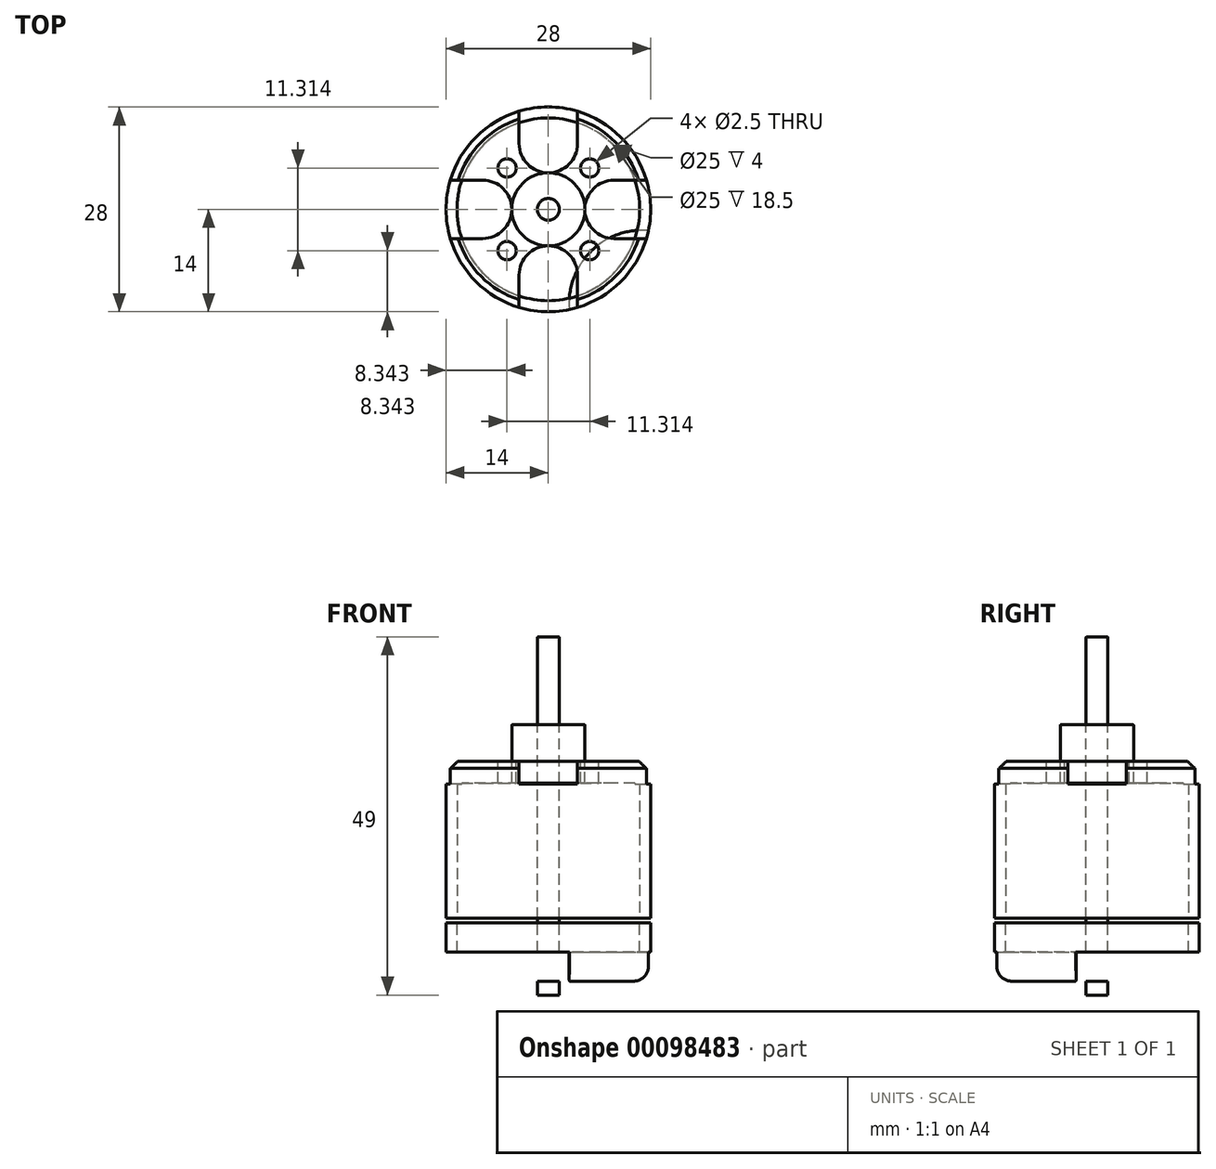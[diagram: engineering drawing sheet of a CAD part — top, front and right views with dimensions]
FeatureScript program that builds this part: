
annotation { "Feature Type Name" : "Feature", "Feature Type Description" : "" }
export const myFeature = defineFeature(function(context is Context, id is Id, definition is map)
    precondition{}
    {
        {
            var Q0;
            Q0=qCreatedBy(makeId("Top.planeOp"),FACE);
            var sketch = newSketch(context, id + "F0", { "sketchPlane" : qUnion([Q0])});
            skCircle(sketch, "E0", {"center": v(0, 0) * mm, "radius": 14 * mm});
            skSolve(sketch);
        }
        {
            var Q0;
            Q0=qSketchRegion(id+"F0",true);
            extrude(context, id + "F1", {"entities" : qUnion([Q0]), "depth" : 21.5 * mm});
        }
        {
            var Q0;
            Q0=makeQuery(id+"F1.opExtrude","CAP_FACE",FACE,{"disambiguationData":[OSD([sQuery(id+"F0.wireOp",EDGE,"E0")])],"isStart":false});
            var sketch = newSketch(context, id + "F2", { "sketchPlane" : qUnion([Q0])});
            skCircle(sketch, "E1", {"center": v(0, 0) * mm, "radius": 5 * mm});
            skSolve(sketch);
        }
        {
            var Q0;
            Q0=qSketchRegion(id+"F2",true);
            extrude(context, id + "F3", {"entities" : qUnion([Q0]), "depth" : 5 * mm});
        }
        {
            var Q0;
            Q0=makeQuery(id+"F1.opExtrude","CAP_FACE",FACE,{"disambiguationData":[OSD([sQuery(id+"F0.wireOp",EDGE,"E0")])],"isStart":true});
            var sketch = newSketch(context, id + "F4", { "sketchPlane" : qUnion([Q0])});
            skCircle(sketch, "E2", {"center": v(0, 0) * mm, "radius": 12.5 * mm});
            skSolve(sketch);
        }
        {
            var Q0;
            Q0=qSketchRegion(id+"F4",true);
            extrude(context, id + "F5", {"entities" : qUnion([Q0]), "operationType" : NewBodyOperationType.REMOVE, "oppositeDirection" : true, "depth" : 18.5 * mm});
        }
        {
            var Q0;
            Q0=makeQuery(id+"F3.opExtrude","CAP_FACE",FACE,{"disambiguationData":[OSD([sQuery(id+"F2.wireOp",EDGE,"E1")])],"isStart":false});
            cPlane(context, id + "F6", {"entities" : qUnion([Q0]), "cplaneType" : CPlaneType.OFFSET, "offset" : 12 * mm, "width" : 150 * mm, "height" : 150 * mm});
        }
        {
            var Q0;
            Q0=qCreatedBy(id+"F6.planeOp",FACE);
            var sketch = newSketch(context, id + "F7", { "sketchPlane" : qUnion([Q0])});
            skCircle(sketch, "E3", {"center": v(0, 0) * mm, "radius": 1.5 * mm});
            skSolve(sketch);
        }
        {
            var Q0;
            Q0=qSketchRegion(id+"F7",true);
            extrude(context, id + "F8", {"entities" : qUnion([Q0]), "oppositeDirection" : true, "depth" : 49 * mm});
        }
        {
            var Q0;
            Q0=makeQuery(id+"F1.opExtrude","CAP_FACE",FACE,{"disambiguationData":[OSD([sQuery(id+"F0.wireOp",EDGE,"E0")])],"isStart":false});
            var sketch = newSketch(context, id + "F9", { "sketchPlane" : qUnion([Q0])});
            skArc(sketch, "E4", {"start": v(-4, 9) * mm, "mid": v(0, 5) * mm, "end": v(4, 9) * mm});
            skLineSegment(sketch, "E5", {"start": v(4, 9) * mm, "end": v(4, 13.42) * mm});
            skLineSegment(sketch, "E6.MirrorCS", {"start": v(-4, 9) * mm, "end": v(-4, 13.42) * mm});
            skArc(sketch, "E7", {"start": v(-4, 13.42) * mm, "mid": v(0, 14) * mm, "end": v(4, 13.42) * mm});
            skArc(sketch, "E8.1.0", {"start": v(-9, -4) * mm, "mid": v(-5, 0) * mm, "end": v(-9, 4) * mm});
            skLineSegment(sketch, "E8.1.1", {"start": v(-9, 4) * mm, "end": v(-13.42, 4) * mm});
            skArc(sketch, "E8.1.2", {"start": v(-13.42, -4) * mm, "mid": v(-14, 0) * mm, "end": v(-13.42, 4) * mm});
            skLineSegment(sketch, "E8.1.3", {"start": v(-9, -4) * mm, "end": v(-13.42, -4) * mm});
            skArc(sketch, "E8.2.0", {"start": v(4, -9) * mm, "mid": v(0, -5) * mm, "end": v(-4, -9) * mm});
            skLineSegment(sketch, "E8.2.1", {"start": v(-4, -9) * mm, "end": v(-4, -13.42) * mm});
            skArc(sketch, "E8.2.2", {"start": v(4, -13.42) * mm, "mid": v(0, -14) * mm, "end": v(-4, -13.42) * mm});
            skLineSegment(sketch, "E8.2.3", {"start": v(4, -9) * mm, "end": v(4, -13.42) * mm});
            skArc(sketch, "E8.3.0", {"start": v(9, 4) * mm, "mid": v(5, 0) * mm, "end": v(9, -4) * mm});
            skLineSegment(sketch, "E8.3.1", {"start": v(9, -4) * mm, "end": v(13.42, -4) * mm});
            skArc(sketch, "E8.3.2", {"start": v(13.42, 4) * mm, "mid": v(14, 0) * mm, "end": v(13.42, -4) * mm});
            skLineSegment(sketch, "E8.3.3", {"start": v(9, 4) * mm, "end": v(13.42, 4) * mm});
            skSolve(sketch);
        }
        {
            var Q0;
            Q0=qSketchRegion(id+"F9",true);
            extrude(context, id + "F10", {"entities" : qUnion([Q0]), "operationType" : NewBodyOperationType.REMOVE, "oppositeDirection" : true, "depth" : 3.12 * mm});
        }
        {
            var Q0;
            {var subQ0=sQuery(id+"F0.wireOp",EDGE,"E0");Q0=makeQuery(id+"F10.boolean.opBoolean","SPLIT",EDGE,{"disambiguationData":[TD([makeQuery(id+"F10.opExtrude","SWEPT_FACE",FACE,{"disambiguationData":[OSD([sQuery(id+"F9.wireOp",EDGE,"E6.MirrorCS")])]})])],"derivedFrom":makeQuery(id+"F1.opExtrude","CAP_EDGE",EDGE,{"disambiguationData":[OSD([subQ0])],"isStart":false})});}
            var Q1;
            {var subQ0=sQuery(id+"F0.wireOp",EDGE,"E0");Q1=makeQuery(id+"F10.boolean.opBoolean","SPLIT",EDGE,{"disambiguationData":[TD([makeQuery(id+"F10.opExtrude","SWEPT_FACE",FACE,{"disambiguationData":[OSD([sQuery(id+"F9.wireOp",EDGE,"E5")])]})])],"derivedFrom":makeQuery(id+"F1.opExtrude","CAP_EDGE",EDGE,{"disambiguationData":[OSD([subQ0])],"isStart":false})});}
            var Q2;
            {var subQ0=sQuery(id+"F0.wireOp",EDGE,"E0");Q2=makeQuery(id+"F10.boolean.opBoolean","SPLIT",EDGE,{"disambiguationData":[TD([makeQuery(id+"F10.opExtrude","SWEPT_FACE",FACE,{"disambiguationData":[OSD([sQuery(id+"F9.wireOp",EDGE,"E8.2.3")])]})])],"derivedFrom":makeQuery(id+"F1.opExtrude","CAP_EDGE",EDGE,{"disambiguationData":[OSD([subQ0])],"isStart":false})});}
            var Q3;
            {var subQ0=sQuery(id+"F0.wireOp",EDGE,"E0");Q3=makeQuery(id+"F10.boolean.opBoolean","SPLIT",EDGE,{"disambiguationData":[TD([makeQuery(id+"F10.opExtrude","SWEPT_FACE",FACE,{"disambiguationData":[OSD([sQuery(id+"F9.wireOp",EDGE,"E8.1.3")])]})])],"derivedFrom":makeQuery(id+"F1.opExtrude","CAP_EDGE",EDGE,{"disambiguationData":[OSD([subQ0])],"isStart":false})});}
            chamfer(context, id + "F11", {"entities" : qUnion([Q0, Q1, Q2, Q3]), "width" : 1 * mm, "tangentPropagation" : true});
        }
        {
            var Q0;
            Q0=makeQuery(id+"F8.opExtrude","CAP_EDGE",EDGE,{"disambiguationData":[OSD([sQuery(id+"F7.wireOp",EDGE,"E3")])],"isStart":true});
            fillet(context, id + "F12", {"entities" : qUnion([Q0]), "radius" : .1 * mm, "tangentPropagation" : true, "allowEdgeOverflow" : false});
        }
        {
            var Q0;
            Q0=makeQuery(id+"F3.opExtrude","CAP_EDGE",EDGE,{"disambiguationData":[OSD([sQuery(id+"F2.wireOp",EDGE,"E1")])],"isStart":false});
            var Q1;
            Q1=makeQuery(id+"F3.opExtrude","CAP_EDGE",EDGE,{"disambiguationData":[OSD([sQuery(id+"F2.wireOp",EDGE,"E1")])],"isStart":true});
            fillet(context, id + "F13", {"entities" : qUnion([Q0, Q1]), "radius" : .1 * mm, "tangentPropagation" : true, "allowEdgeOverflow" : false});
        }
        {
            var Q0;
            Q0=makeQuery(id+"F1.opExtrude","CAP_FACE",FACE,{"disambiguationData":[OSD([sQuery(id+"F0.wireOp",EDGE,"E0")])],"isStart":true});
            var sketch = newSketch(context, id + "F14", { "sketchPlane" : qUnion([Q0])});
            skCircle(sketch, "E9.0", {"center": v(0, 0) * mm, "radius": 14 * mm});
            skCircle(sketch, "E9.1", {"center": v(0, 0) * mm, "radius": 12.5 * mm});
            skSolve(sketch);
        }
        {
            var Q0;
            Q0=qSketchRegion(id+"F14",true);
            extrude(context, id + "F15", {"entities" : qUnion([Q0]), "depth" : 8 * mm});
        }
        {
            var Q0;
            Q0=makeQuery(id+"F15.opExtrude","SWEPT_BODY",BODY,{"disambiguationData":[OSD([sQuery(id+"F14.wireOp",EDGE,"E9.0"),sQuery(id+"F14.wireOp",EDGE,"E9.1")])]});
            transform(context, id + "F16", {"entities" : qUnion([Q0]), "transformType" : TransformType.TRANSLATION_3D, "dx" : 0 * mm, "dy" : 0 * mm, "dz" : -.6 * mm, "makeCopy" : false});
        }
        {
            var Q0;
            Q0=makeQuery(id+"F15.opExtrude","CAP_FACE",FACE,{"disambiguationData":[OSD([sQuery(id+"F14.wireOp",EDGE,"E9.0"),sQuery(id+"F14.wireOp",EDGE,"E9.1")])],"isStart":false});
            var sketch = newSketch(context, id + "F17", { "sketchPlane" : qUnion([Q0])});
            skCircle(sketch, "E10.0", {"center": v(0, 0) * mm, "radius": 12.5 * mm});
            skCircle(sketch, "E11", {"center": v(0, 0) * mm, "radius": 8 * mm, "construction": true});
            skCircle(sketch, "E12", {"center": v(-8, 0) * mm, "radius": 1.25 * mm});
            skCircle(sketch, "E13.1.0", {"center": v(0, -8) * mm, "radius": 1.25 * mm});
            skCircle(sketch, "E13.2.0", {"center": v(8, 0) * mm, "radius": 1.25 * mm});
            skCircle(sketch, "E13.3.0", {"center": v(0, 8) * mm, "radius": 1.25 * mm});
            skSolve(sketch);
        }
        {
            var Q0;
            Q0=qSketchRegion(id+"F17",true);
            extrude(context, id + "F18", {"entities" : qUnion([Q0]), "oppositeDirection" : true, "depth" : 4 * mm});
        }
        {
            var Q0;
            Q0=makeQuery(id+"F18.opExtrude","SWEPT_BODY",BODY,{"disambiguationData":[OSD([sQuery(id+"F17.wireOp",EDGE,"E10.0")])]});
            var Q1;
            Q1=makeQuery(id+"F15.opExtrude","SWEPT_BODY",BODY,{"disambiguationData":[OSD([sQuery(id+"F14.wireOp",EDGE,"E9.0"),sQuery(id+"F14.wireOp",EDGE,"E9.1")])]});
            booleanBodies(context, id + "F19", {"operationType" : BooleanOperationType.UNION, "tools" : qUnion([Q0, Q1])});
        }
        {
            var Q0;
            Q0=makeQuery(id+"F19.opBoolean","MERGE",FACE,{"derivedFrom":[makeQuery(id+"F15.opExtrude","CAP_FACE",FACE,{"disambiguationData":[OSD([sQuery(id+"F14.wireOp",EDGE,"E9.0"),sQuery(id+"F14.wireOp",EDGE,"E9.1")])],"isStart":false}),makeQuery(id+"F18.opExtrude","CAP_FACE",FACE,{"disambiguationData":[OSD([sQuery(id+"F17.wireOp",EDGE,"E10.0"),sQuery(id+"F17.wireOp",EDGE,"E12"),sQuery(id+"F17.wireOp",EDGE,"E13.1.0"),sQuery(id+"F17.wireOp",EDGE,"E13.2.0"),sQuery(id+"F17.wireOp",EDGE,"E13.3.0")])],"isStart":true})]});
            var sketch = newSketch(context, id + "F20", { "sketchPlane" : qUnion([Q0])});
            skLineSegment(sketch, "E14", {"start": v(0, 0) * mm, "end": v(-16.49, 16.49) * mm, "construction": true});
            skArc(sketch, "E15", {"start": v(-13.7, 2.88) * mm, "mid": v(-5.79, 5.79) * mm, "end": v(-2.88, 13.7) * mm});
            skLineSegment(sketch, "E16", {"start": v(-2.85, 0) * mm, "end": v(-2.85, 15.2) * mm, "construction": true});
            skArc(sketch, "E17", {"start": v(-13.7, 2.88) * mm, "mid": v(-9.9, 9.9) * mm, "end": v(-2.88, 13.7) * mm});
            skArc(sketch, "E18.MirrorCS", {"start": v(13.7, 2.88) * mm, "mid": v(5.79, 5.79) * mm, "end": v(2.88, 13.7) * mm});
            skArc(sketch, "E19.MirrorCS", {"start": v(13.7, 2.88) * mm, "mid": v(9.9, 9.9) * mm, "end": v(2.88, 13.7) * mm});
            skArc(sketch, "E20.MirrorCS", {"start": v(-13.7, -2.88) * mm, "mid": v(-9.9, -9.9) * mm, "end": v(-2.88, -13.7) * mm});
            skArc(sketch, "E21.MirrorCS", {"start": v(-13.7, -2.88) * mm, "mid": v(-5.79, -5.79) * mm, "end": v(-2.88, -13.7) * mm});
            skArc(sketch, "E22.MirrorCS", {"start": v(13.7, -2.88) * mm, "mid": v(5.79, -5.79) * mm, "end": v(2.88, -13.7) * mm});
            skArc(sketch, "E23.MirrorCS", {"start": v(13.7, -2.88) * mm, "mid": v(9.9, -9.9) * mm, "end": v(2.88, -13.7) * mm});
            skSolve(sketch);
        }
        {
            var Q0;
            Q0=makeQuery(id+"F20.imprint","IMPRINT",FACE,{"disambiguationData":[TD([[makeQuery(id+"F20.imprint","IMPRINT",EDGE,{"derivedFrom":sQuery(id+"F20.wireOp",EDGE,"E15")}),1.0]])]});
            var Q1;
            Q1=makeQuery(id+"F20.imprint","IMPRINT",FACE,{"disambiguationData":[TD([[makeQuery(id+"F20.imprint","IMPRINT",EDGE,{"derivedFrom":sQuery(id+"F20.wireOp",EDGE,"E18.MirrorCS")}),-1.0]])]});
            var Q2;
            Q2=makeQuery(id+"F20.imprint","IMPRINT",FACE,{"disambiguationData":[TD([[makeQuery(id+"F20.imprint","IMPRINT",EDGE,{"derivedFrom":sQuery(id+"F20.wireOp",EDGE,"E20.MirrorCS")}),-1.0]])]});
            var Q3;
            Q3=makeQuery(id+"F20.imprint","IMPRINT",FACE,{"disambiguationData":[TD([[makeQuery(id+"F20.imprint","IMPRINT",EDGE,{"derivedFrom":sQuery(id+"F20.wireOp",EDGE,"E22.MirrorCS")}),1.0]])]});
            extrude(context, id + "F21", {"entities" : qUnion([Q0, Q1, Q2, Q3]), "operationType" : NewBodyOperationType.REMOVE, "oppositeDirection" : true, "depth" : 4 * mm});
        }
        {
            var Q0;
            {var subQ0=sQuery(id+"F14.wireOp",EDGE,"E9.0");Q0=makeQuery(id+"F21.boolean.opBoolean","SPLIT",EDGE,{"disambiguationData":[TD([makeQuery(id+"F15.opExtrude","SWEPT_FACE",FACE,{"disambiguationData":[OSD([subQ0])]}),makeQuery(id+"F15.opExtrude","CAP_FACE",FACE,{"disambiguationData":[OSD([subQ0,sQuery(id+"F14.wireOp",EDGE,"E9.1")])],"isStart":false}),makeQuery(id+"F18.opExtrude","CAP_FACE",FACE,{"disambiguationData":[OSD([sQuery(id+"F17.wireOp",EDGE,"E10.0"),sQuery(id+"F17.wireOp",EDGE,"E12"),sQuery(id+"F17.wireOp",EDGE,"E13.1.0"),sQuery(id+"F17.wireOp",EDGE,"E13.2.0"),sQuery(id+"F17.wireOp",EDGE,"E13.3.0")])],"isStart":true}),makeQuery(id+"F21.opExtrude","SWEPT_FACE",FACE,{"disambiguationData":[OSD([sQuery(id+"F20.wireOp",EDGE,"E15")])]}),makeQuery(id+"F21.opExtrude","SWEPT_FACE",FACE,{"disambiguationData":[OSD([sQuery(id+"F20.wireOp",EDGE,"E21.MirrorCS")])]})])],"derivedFrom":makeQuery(id+"F15.opExtrude","CAP_EDGE",EDGE,{"disambiguationData":[OSD([subQ0])],"isStart":false})});}
            var Q1;
            {var subQ0=sQuery(id+"F14.wireOp",EDGE,"E9.0");Q1=makeQuery(id+"F21.boolean.opBoolean","SPLIT",EDGE,{"disambiguationData":[TD([makeQuery(id+"F15.opExtrude","SWEPT_FACE",FACE,{"disambiguationData":[OSD([subQ0])]}),makeQuery(id+"F15.opExtrude","CAP_FACE",FACE,{"disambiguationData":[OSD([subQ0,sQuery(id+"F14.wireOp",EDGE,"E9.1")])],"isStart":false}),makeQuery(id+"F18.opExtrude","CAP_FACE",FACE,{"disambiguationData":[OSD([sQuery(id+"F17.wireOp",EDGE,"E10.0"),sQuery(id+"F17.wireOp",EDGE,"E12"),sQuery(id+"F17.wireOp",EDGE,"E13.1.0"),sQuery(id+"F17.wireOp",EDGE,"E13.2.0"),sQuery(id+"F17.wireOp",EDGE,"E13.3.0")])],"isStart":true}),makeQuery(id+"F21.opExtrude","SWEPT_FACE",FACE,{"disambiguationData":[OSD([sQuery(id+"F20.wireOp",EDGE,"E15")])]}),makeQuery(id+"F21.opExtrude","SWEPT_FACE",FACE,{"disambiguationData":[OSD([sQuery(id+"F20.wireOp",EDGE,"E18.MirrorCS")])]})])],"derivedFrom":makeQuery(id+"F15.opExtrude","CAP_EDGE",EDGE,{"disambiguationData":[OSD([subQ0])],"isStart":false})});}
            var Q2;
            {var subQ0=sQuery(id+"F14.wireOp",EDGE,"E9.0");Q2=makeQuery(id+"F21.boolean.opBoolean","SPLIT",EDGE,{"disambiguationData":[TD([makeQuery(id+"F15.opExtrude","SWEPT_FACE",FACE,{"disambiguationData":[OSD([subQ0])]}),makeQuery(id+"F15.opExtrude","CAP_FACE",FACE,{"disambiguationData":[OSD([subQ0,sQuery(id+"F14.wireOp",EDGE,"E9.1")])],"isStart":false}),makeQuery(id+"F18.opExtrude","CAP_FACE",FACE,{"disambiguationData":[OSD([sQuery(id+"F17.wireOp",EDGE,"E10.0"),sQuery(id+"F17.wireOp",EDGE,"E12"),sQuery(id+"F17.wireOp",EDGE,"E13.1.0"),sQuery(id+"F17.wireOp",EDGE,"E13.2.0"),sQuery(id+"F17.wireOp",EDGE,"E13.3.0")])],"isStart":true}),makeQuery(id+"F21.opExtrude","SWEPT_FACE",FACE,{"disambiguationData":[OSD([sQuery(id+"F20.wireOp",EDGE,"E18.MirrorCS")])]}),makeQuery(id+"F21.opExtrude","SWEPT_FACE",FACE,{"disambiguationData":[OSD([sQuery(id+"F20.wireOp",EDGE,"E22.MirrorCS")])]})])],"derivedFrom":makeQuery(id+"F15.opExtrude","CAP_EDGE",EDGE,{"disambiguationData":[OSD([subQ0])],"isStart":false})});}
            var Q3;
            {var subQ0=sQuery(id+"F14.wireOp",EDGE,"E9.0");Q3=makeQuery(id+"F21.boolean.opBoolean","SPLIT",EDGE,{"disambiguationData":[TD([makeQuery(id+"F15.opExtrude","SWEPT_FACE",FACE,{"disambiguationData":[OSD([subQ0])]}),makeQuery(id+"F15.opExtrude","CAP_FACE",FACE,{"disambiguationData":[OSD([subQ0,sQuery(id+"F14.wireOp",EDGE,"E9.1")])],"isStart":false}),makeQuery(id+"F18.opExtrude","CAP_FACE",FACE,{"disambiguationData":[OSD([sQuery(id+"F17.wireOp",EDGE,"E10.0"),sQuery(id+"F17.wireOp",EDGE,"E12"),sQuery(id+"F17.wireOp",EDGE,"E13.1.0"),sQuery(id+"F17.wireOp",EDGE,"E13.2.0"),sQuery(id+"F17.wireOp",EDGE,"E13.3.0")])],"isStart":true}),makeQuery(id+"F21.opExtrude","SWEPT_FACE",FACE,{"disambiguationData":[OSD([sQuery(id+"F20.wireOp",EDGE,"E21.MirrorCS")])]}),makeQuery(id+"F21.opExtrude","SWEPT_FACE",FACE,{"disambiguationData":[OSD([sQuery(id+"F20.wireOp",EDGE,"E22.MirrorCS")])]})])],"derivedFrom":makeQuery(id+"F15.opExtrude","CAP_EDGE",EDGE,{"disambiguationData":[OSD([subQ0])],"isStart":false})});}
            fillet(context, id + "F22", {"entities" : qUnion([Q0, Q1, Q2, Q3]), "radius" : 2 * mm, "tangentPropagation" : true, "allowEdgeOverflow" : false});
        }
        {
            var Q0;
            Q0=makeQuery(id+"F19.opBoolean","MERGE",FACE,{"derivedFrom":[makeQuery(id+"F15.opExtrude","CAP_FACE",FACE,{"disambiguationData":[OSD([sQuery(id+"F14.wireOp",EDGE,"E9.0"),sQuery(id+"F14.wireOp",EDGE,"E9.1")])],"isStart":false}),makeQuery(id+"F18.opExtrude","CAP_FACE",FACE,{"disambiguationData":[OSD([sQuery(id+"F17.wireOp",EDGE,"E10.0"),sQuery(id+"F17.wireOp",EDGE,"E12"),sQuery(id+"F17.wireOp",EDGE,"E13.1.0"),sQuery(id+"F17.wireOp",EDGE,"E13.2.0"),sQuery(id+"F17.wireOp",EDGE,"E13.3.0")])],"isStart":true})]});
            var sketch = newSketch(context, id + "F23", { "sketchPlane" : qUnion([Q0])});
            skCircle(sketch, "E24", {"center": v(0, 0) * mm, "radius": 5 * mm});
            skCircle(sketch, "E25", {"center": v(0, 0) * mm, "radius": 1.5 * mm});
            skSolve(sketch);
        }
        {
            var Q0;
            Q0=qSketchRegion(id+"F23",true);
            extrude(context, id + "F24", {"entities" : qUnion([Q0]), "operationType" : NewBodyOperationType.REMOVE, "oppositeDirection" : true, "depth" : 1 * mm});
        }
        {
            var Q0;
            Q0=makeQuery(id+"F1.opExtrude","CAP_FACE",FACE,{"disambiguationData":[OSD([sQuery(id+"F0.wireOp",EDGE,"E0")])],"isStart":false});
            var sketch = newSketch(context, id + "F25", { "sketchPlane" : qUnion([Q0])});
            skCircle(sketch, "E26", {"center": v(0, 0) * mm, "radius": 8 * mm, "construction": true});
            skCircle(sketch, "E27", {"center": v(5.66, 5.66) * mm, "radius": 1.25 * mm});
            skLineSegment(sketch, "E28", {"start": v(0, 0) * mm, "end": v(5.66, 5.66) * mm, "construction": true});
            skCircle(sketch, "E29.1.0", {"center": v(-5.66, 5.66) * mm, "radius": 1.25 * mm});
            skCircle(sketch, "E29.2.0", {"center": v(-5.66, -5.66) * mm, "radius": 1.25 * mm});
            skCircle(sketch, "E29.3.0", {"center": v(5.66, -5.66) * mm, "radius": 1.25 * mm});
            skSolve(sketch);
        }
        {
            var Q0;
            Q0 = qSketchRegion(id + "F25", true);
            extrude(context, id + "F26", {"entities" : qUnion([Q0]), "operationType" : NewBodyOperationType.REMOVE, "endBound" : BoundingType.UP_TO_NEXT, "oppositeDirection" : true, "depth" : 25 * mm});
        }
    });
